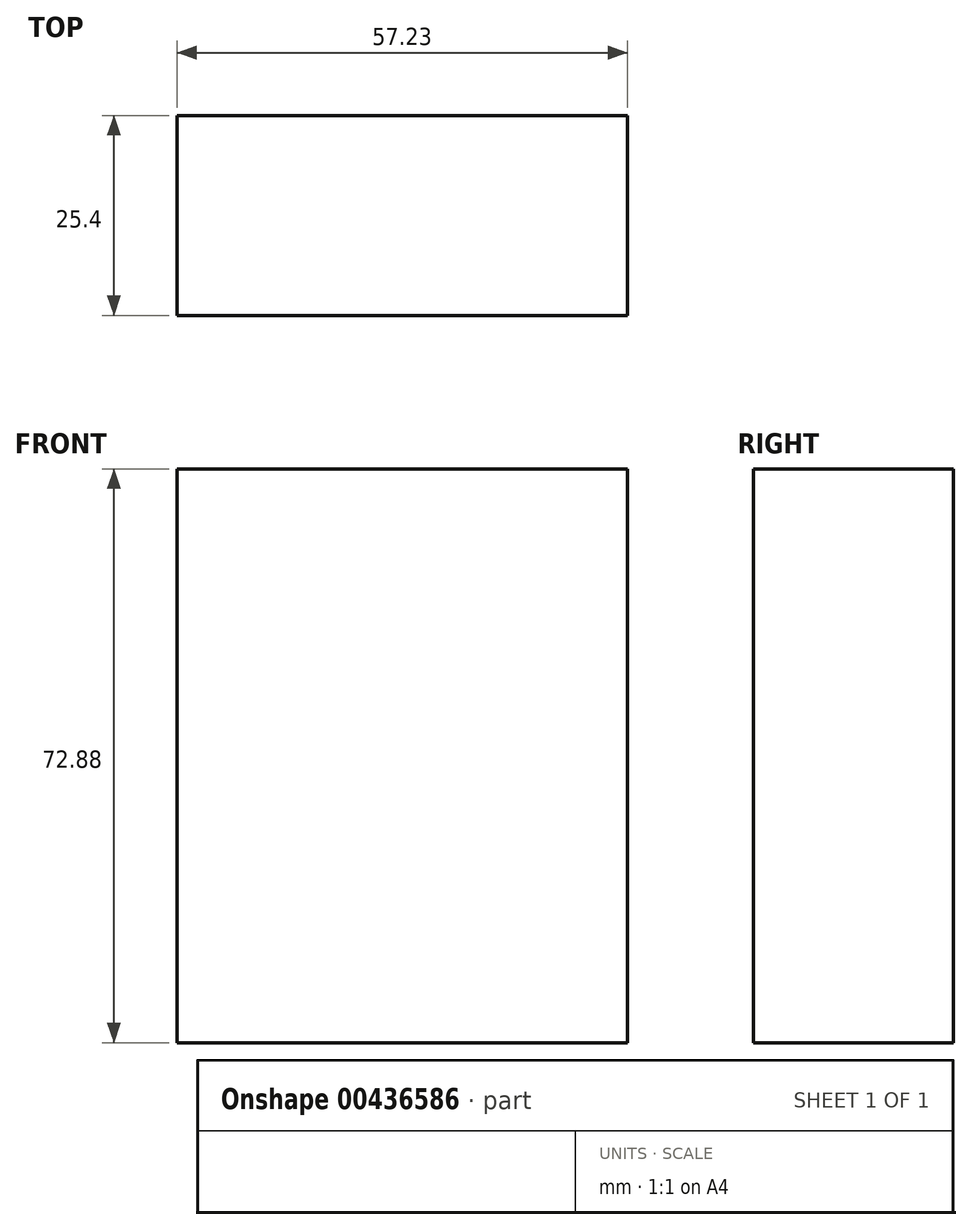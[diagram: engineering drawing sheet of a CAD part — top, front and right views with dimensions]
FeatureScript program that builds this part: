
annotation { "Feature Type Name" : "Feature", "Feature Type Description" : "" }
export const myFeature = defineFeature(function(context is Context, id is Id, definition is map)
    precondition{}
    {
        {
            var Q0;
            Q0=qCreatedBy(makeId("Front.planeOp"),FACE);
            var sketch = newSketch(context, id + "F0", { "sketchPlane" : qUnion([Q0])});
            skLineSegment(sketch, "E0.bottom", {"start": v(0, 36.1) * mm, "end": v(57.23, 36.1) * mm});
            skLineSegment(sketch, "E0.top", {"start": v(0, 0) * mm, "end": v(57.23, 0) * mm});
            skLineSegment(sketch, "E0.left", {"start": v(0, 36.1) * mm, "end": v(0, 0) * mm});
            skLineSegment(sketch, "E0.right", {"start": v(57.23, 36.1) * mm, "end": v(57.23, 0) * mm});
            skLineSegment(sketch, "E1", {"start": v(0, 36.1) * mm, "end": v(-48.12, 0) * mm});
            skLineSegment(sketch, "E2", {"start": v(-48.12, 0) * mm, "end": v(0, -37.03) * mm});
            skLineSegment(sketch, "E3.top", {"start": v(0, -36.8) * mm, "end": v(57.23, -36.8) * mm});
            skLineSegment(sketch, "E3.left", {"start": v(0, 0) * mm, "end": v(0, -36.8) * mm});
            skLineSegment(sketch, "E3.right", {"start": v(57.23, 0) * mm, "end": v(57.23, -36.8) * mm});
            skSolve(sketch);
        }
        {
            var Q0;
            Q0=makeQuery(id+"F0.imprint","IMPRINT",FACE,{"disambiguationData":[TD([[makeQuery(id+"F0.imprint","IMPRINT",EDGE,{"derivedFrom":sQuery(id+"F0.wireOp",EDGE,"E0.bottom")}),-1.0]])]});
            var Q1;
            Q1=makeQuery(id+"F0.imprint","IMPRINT",FACE,{"disambiguationData":[TD([[makeQuery(id+"F0.imprint","IMPRINT",EDGE,{"derivedFrom":sQuery(id+"F0.wireOp",EDGE,"E0.top")}),-1.0]])]});
            extrude(context, id + "F1", {"entities" : qUnion([Q0, Q1]), "depth" : 25.4 * mm});
        }
    });
